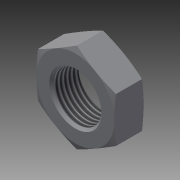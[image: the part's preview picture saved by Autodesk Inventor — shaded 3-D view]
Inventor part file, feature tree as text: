
AUTODESK INVENTOR PART (.ipt)
format: ipt  version: 2014 SP2 (Build 180246200, 246)  size: 157,184 bytes
history: native  units: in
note: dims shown in document units (in); Inventor stores cm internally (conversion verified against a paired STEP export)
features: other x70, sketch x3, revolve x2, extrude x1, thread x1
ambient origin geometry x8: Origin, YZ Plane, XZ Plane, XY Plane, X Axis, Y Axis, Z Axis, Center Point
bodies: Solid1 (feature_tree)
feature tree (77):
  sketch  "Sketch_8"  dims[d0=360.0deg d1=0.42in d2=0.0in]
  sketch  "Sketch_10"  dims[d3=360.0deg d4=0.3523in d5=0.0in]
  revolve  "Revolution1"  [1 undecoded]
  extrude  "Extrusion1"  Depth=0.3523in TaperAngle=0.0deg
  revolve  "Revolution2"  [1 undecoded]
  thread  "Thread1"  [1 undecoded]
  other  "NUT_XY"
  other  "NUT_YZ"
  other  "NUT_ZX"
  other  "NUT_X"
  other  "NUT_Y"
  other  "NUT_Z"
  other  "NUT_Center"
  other  "a1_XY"
  other  "a1_YZ"
  other  "a1_ZX"
  other  "a1_X"
  other  "a1_Y"
  other  "a1_Z"
  other  "a1_Center"
  other  "a2_XY"
  other  "a2_YZ"
  other  "a2_ZX"
  other  "a2_X"
  other  "a2_Y"
  other  "a2_Z"
  other  "a2_Center"
  other  "b1_XY"
  other  "b1_YZ"
  other  "b1_ZX"
  other  "b1_X"
  other  "b1_Y"
  other  "b1_Z"
  other  "b1_Center"
  other  "b2_XY"
  other  "b2_YZ"
  other  "b2_ZX"
  other  "b2_X"
  other  "b2_Y"
  other  "b2_Z"
  other  "b2_Center"
  other  "e_XY"
  other  "e_YZ"
  other  "e_ZX"
  other  "e_X"
  other  "e_Y"
  other  "e_Z"
  other  "e_Center"
  other  "ol1_XY"
  other  "ol1_YZ"
  other  "ol1_ZX"
  other  "ol1_X"
  other  "ol1_Y"
  other  "ol1_Z"
  other  "ol1_Center"
  other  "ol2_XY"
  other  "ol2_YZ"
  other  "ol2_ZX"
  other  "ol2_X"
  other  "ol2_Y"
  other  "ol2_Z"
  other  "ol2_Center"
  other  "th1_XY"
  other  "th1_YZ"
  other  "th1_ZX"
  other  "th1_X"
  other  "th1_Y"
  other  "th1_Z"
  other  "th1_Center"
  other  "th2_XY"
  other  "th2_YZ"
  other  "th2_ZX"
  other  "th2_X"
  other  "th2_Y"
  other  "th2_Z"
  other  "th2_Center"
  sketch  "Sketch_11"  dims[d6=0.0in d7=0.0in d8=0.0in]
note: 3 required parameter values undecoded (feature->parameter linkage not recoverable at this tier; creation-order binding heuristic only, values carry confidence <= 0.55)